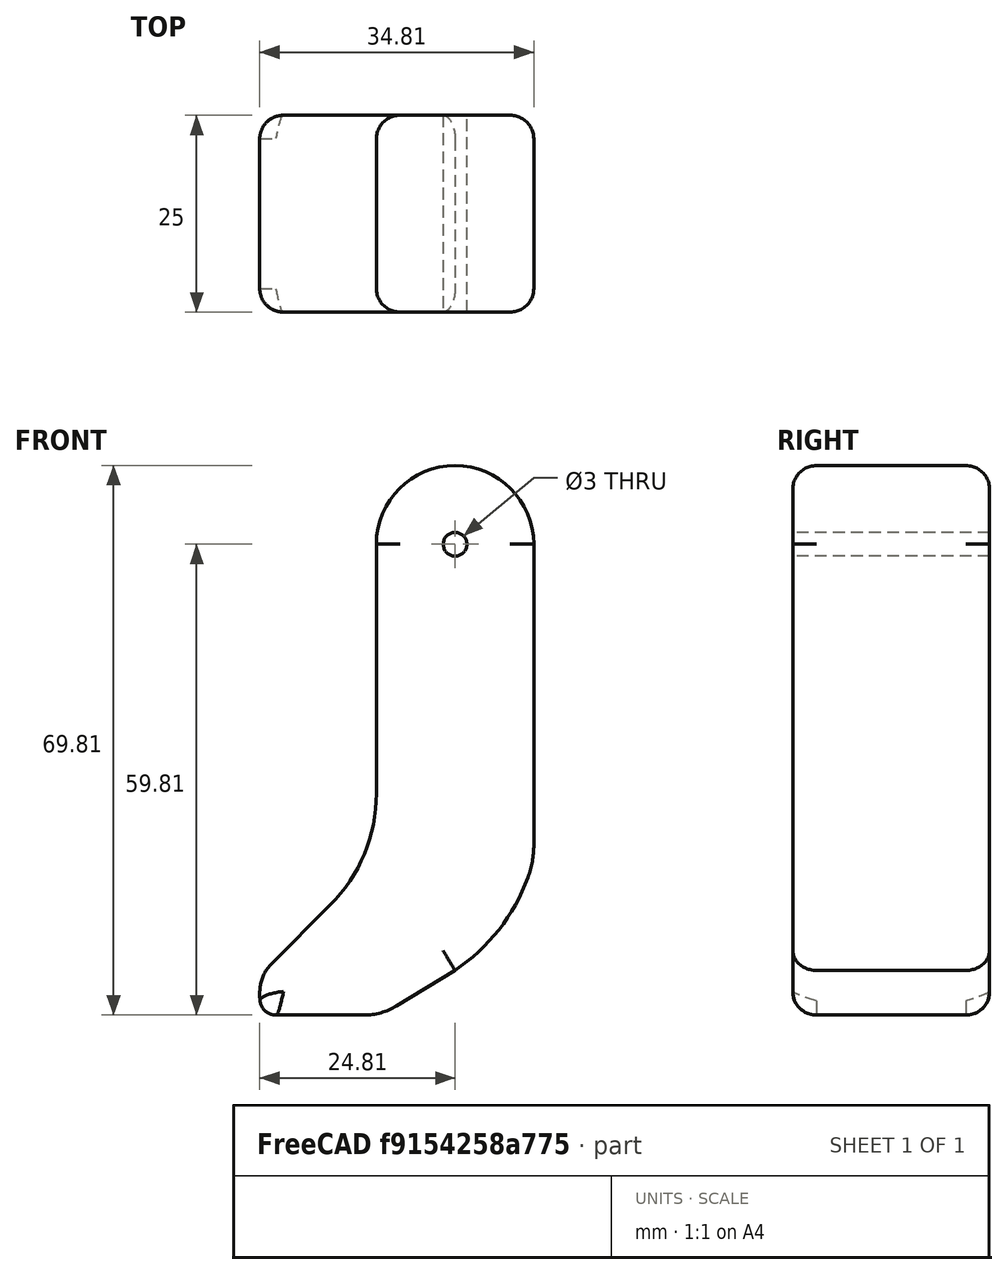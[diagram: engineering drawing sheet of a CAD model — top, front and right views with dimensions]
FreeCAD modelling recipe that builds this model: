
FCSTD DOCUMENT  (FreeCAD 1.0R38806 (Git))
Label: pata
License: All rights reserved
LicenseURL: https://en.wikipedia.org/wiki/All_rights_reserved
objects: PartDesign::Fillet×7, TechDraw::DrawProjGroupItem×5, TechDraw::DrawViewDimension×5, Sketcher::SketchObject×2, TechDraw::DrawProjGroup×2, PartDesign::Pad×1, TechDraw::DrawSVGTemplate×1, PartDesign::Pocket×1, PartDesign::Body×1, App::Part×1, TechDraw::DrawPage×1
note: 37 computed .brp shape members not serialized (recipe doc carries the construction recipe); baked Part::Feature solids carry a one-line shape summary decoded from their .brp

FEATURE [Sketcher::SketchObject] Sketch  label="Sketch_pata_15mm"
  ArcFitTolerance = 1e-06
  AttachmentSupport = -> [XZ_Plane001]
  FullyConstrained = false
  MakeInternals = false
  MapMode = 5
  Placement = pos=(0,0,0) rot=(1,0,0;1.5708rad)
  sketch-geometry (8):
    g0: LineSegment StartX=-10.0001 StartY=23.058 StartZ=0 EndX=-10.0001 EndY=-16.942 EndZ=0
    g1: LineSegment StartX=9.99968 StartY=23.058 StartZ=0 EndX=9.99968 EndY=-16.942 EndZ=0
    g2: LineSegment StartX=-10.0001 StartY=-16.942 StartZ=0 EndX=-24.1423 EndY=-31.0842 EndZ=0
    g3: ArcOfCircle CenterX=-17.3511 CenterY=-34.1744 CenterZ=0 NormalX=0 NormalY=0 NormalZ=1 AngleXU=0 Radius=7.46124 StartAngle=2.71455 EndAngle=3.49995
    g4: LineSegment StartX=-24.3383 StartY=-36.7914 StartZ=0 EndX=-9.33834 EndY=-36.7914 EndZ=0
    g5: LineSegment StartX=-9.33834 StartY=-36.7914 StartZ=0 EndX=-1.8e-15 EndY=-31.1116 EndZ=0
    g6: ArcOfCircle CenterX=-13.6431 CenterY=-10.8702 CenterZ=0 NormalX=0 NormalY=0 NormalZ=1 AngleXU=0 Radius=24.41 StartAngle=5.30546 EndAngle=6.0318
    g7: ArcOfCircle CenterX=-0.000231101 CenterY=23.0162 CenterZ=0 NormalX=0 NormalY=0 NormalZ=1 AngleXU=0 Radius=10 StartAngle=0.00417804 EndAngle=3.13741
  constraints (21):
    c: Distance(g0) = 40
    c: Vertical(g0)
    c: Distance(g1) = 40
    c: Vertical(g1)
    c: Distance(g2) = 20
    c: Angle(g-1,g2) = -2.35619
    c: Coincident(g2,g0)
    c: Angle(g3) = 0.785398
    c: Coincident(g3,g2)
    c: Distance(g4) = 15
    c: Horizontal(g4)
    c: Coincident(g4,g3)
    c: Coincident(g5,g4)
    c: PointOnObject(g5,g-2)
    c: Coincident(g6,g5)
    c: Coincident(g6,g1)
    c: Coincident(g7,g1)
    c: Coincident(g7,g0)
    c: Radius(g7) = 10
    c: Distance(g5,g5) = 10.93
    c: Radius(g6) = 24.41
FEATURE [PartDesign::Pad] Pad
  Direction = (0,-1,2e-16)
  Length = 25
  Length2 = 10
  Placement = pos=(0,0,0) rot=(1,0,0;1.5708rad)
  Profile = -> Sketch
  ReferenceAxis = -> Sketch [N_Axis]
  Refine = true
  Suppressed = false
  Type = 0
FEATURE [PartDesign::Fillet] Fillet
  Base = -> Pad [Edge11]
  BaseFeature = -> Pad
  Placement = pos=(0,0,0) rot=(1,0,0;1.5708rad)
  Radius = 2
  Refine = true
  SupportTransform = false
  Suppressed = false
  UseAllEdges = false
FEATURE [PartDesign::Fillet] Fillet001
  Base = -> Fillet [Edge23]
  BaseFeature = -> Fillet
  Placement = pos=(0,0,0) rot=(1,0,0;1.5708rad)
  Radius = 8
  Refine = true
  SupportTransform = false
  Suppressed = false
  UseAllEdges = false
FEATURE [PartDesign::Fillet] Fillet002
  Base = -> Fillet001 [Edge20]
  BaseFeature = -> Fillet001
  Placement = pos=(0,0,0) rot=(1,0,0;1.5708rad)
  Radius = 5
  Refine = true
  SupportTransform = false
  Suppressed = false
  UseAllEdges = false
FEATURE [PartDesign::Fillet] Fillet003
  Base = -> Fillet002 [Edge31]
  BaseFeature = -> Fillet002
  Placement = pos=(0,0,0) rot=(1,0,0;1.5708rad)
  Radius = 12
  Refine = true
  SupportTransform = false
  Suppressed = false
  UseAllEdges = false
FEATURE [PartDesign::Fillet] Fillet004
  Base = -> Fillet003 [Edge22]
  BaseFeature = -> Fillet003
  Placement = pos=(0,0,0) rot=(1,0,0;1.5708rad)
  Radius = 20
  Refine = true
  SupportTransform = false
  Suppressed = false
  UseAllEdges = false
FEATURE [PartDesign::Fillet] Fillet005
  Base = -> Fillet004 [Edge20]
  BaseFeature = -> Fillet004
  Placement = pos=(0,0,0) rot=(1,0,0;1.5708rad)
  Radius = 3
  Refine = true
  SupportTransform = false
  Suppressed = false
  UseAllEdges = false
FEATURE [PartDesign::Fillet] Fillet006
  Base = -> Fillet005 [Edge11]
  BaseFeature = -> Fillet005
  Placement = pos=(0,0,0) rot=(1,0,0;1.5708rad)
  Radius = 3
  Refine = true
  SupportTransform = false
  Suppressed = false
  UseAllEdges = false
FEATURE [TechDraw::DrawSVGTemplate] Template
  EditableTexts = approval_person=Mecatrónica; creator=A.Mrtz, N.Grc, T.Marí; date_of_issue=12/14/24; document_status=In preparation; document_type=Assembly Drawing; drawing_number=DN; general_tolerances=ISO 2768-m; language_code=EN; part_material=Stainless steel Mat.No. 1.4301; responsible_department=RD; revision_index=AAA; sheet_number=1 / 1; sheet_scale=1 : 1; title=Pierna_ajolote
  Height = 297
  Orientation = 1
  Template = <path>
  Width = 420
FEATURE [Sketcher::SketchObject] Sketch001
  ArcFitTolerance = 1e-06
  AttachmentSupport = -> [Fillet006]
  FullyConstrained = false
  MakeInternals = false
  MapMode = 5
  Placement = pos=(0,-25,0) rot=(1,0,0;1.5708rad)
  sketch-geometry (1):
    g0: Circle CenterX=0 CenterY=23.02 CenterZ=0 NormalX=0 NormalY=0 NormalZ=1 AngleXU=0 Radius=1.5
  constraints (2):
    c: Diameter(g0) = 3
    c: PointOnObject(g0,g-2)
FEATURE [PartDesign::Pocket] Pocket
  BaseFeature = -> Fillet006
  Direction = (0,1,-2e-16)
  Length = 5
  Length2 = 5
  Placement = pos=(0,0,0) rot=(1,0,0;1.5708rad)
  Profile = -> Sketch001
  ReferenceAxis = -> Sketch001 [N_Axis]
  Refine = true
  Suppressed = false
  Type = 1
FEATURE [PartDesign::Body] Body  label="Pata"
  AllowCompound = false
  Group = -> [Sketch,Pad,Fillet,Fillet001,Fillet002,Fillet003,Fillet004,Fillet005,Fillet006,Sketch001,Pocket]
  Origin = -> Origin001
  Tip = -> Pocket
FEATURE [App::Part] Part  label="Pata001"
  Group = -> [Body]
  Origin = -> Origin
FEATURE [TechDraw::DrawProjGroupItem] ProjItem003  label="Top"
  CoarseView = false
  Direction = (0,0,1)
  Focus = 100
  HardHidden = false
  IsoCount = 0
  IsoHidden = false
  IsoVisible = false
  LockPosition = false
  Perspective = false
  Rotation = 0
  RotationVector = (1,0,0)
  ScaleType = 0
  ScrubCount = 1
  SeamHidden = false
  SeamVisible = false
  SmoothHidden = false
  SmoothVisible = true
  Source = -> [Body]
  Type = 4
  X = 0
  XDirection = (1,0,0)
  Y = -109.808
FEATURE [TechDraw::DrawProjGroupItem] ProjItem  label="Front"
  CoarseView = false
  Direction = (0,-1,0)
  Focus = 100
  HardHidden = false
  IsoCount = 0
  IsoHidden = false
  IsoVisible = false
  LockPosition = true
  Perspective = false
  Rotation = 0
  RotationVector = (1,0,0)
  Scale = 2
  ScaleType = 2
  ScrubCount = 1
  SeamHidden = false
  SeamVisible = false
  SmoothHidden = false
  SmoothVisible = true
  Source = -> [Body]
  Type = 0
  X = 0
  XDirection = (1,0,0)
  Y = 0
FEATURE [TechDraw::DrawProjGroupItem] ProjItem004  label="Top001"
  CoarseView = false
  Direction = (0,0,1)
  Focus = 100
  HardHidden = false
  IsoCount = 0
  IsoHidden = false
  IsoVisible = false
  LockPosition = false
  Perspective = false
  Rotation = 0
  RotationVector = (1,0,0)
  Scale = 2
  ScaleType = 2
  ScrubCount = 1
  SeamHidden = false
  SeamVisible = false
  SmoothHidden = false
  SmoothVisible = true
  Source = -> [Body]
  Type = 4
  X = 0
  XDirection = (1,0,0)
  Y = -109.808
FEATURE [TechDraw::DrawProjGroupItem] ProjItem005  label="Right"
  CoarseView = false
  Direction = (1,-1e-16,0)
  Focus = 100
  HardHidden = false
  IsoCount = 0
  IsoHidden = false
  IsoVisible = false
  LockPosition = false
  Perspective = false
  Rotation = 0
  RotationVector = (1,0,0)
  Scale = 2
  ScaleType = 2
  ScrubCount = 1
  SeamHidden = false
  SeamVisible = false
  SmoothHidden = false
  SmoothVisible = true
  Source = -> [Body]
  Type = 2
  X = -74.812
  XDirection = (1e-16,1,0)
  Y = 0
FEATURE [TechDraw::DrawProjGroup] ProjGroup
  Anchor = -> ProjItem
  AutoDistribute = true
  LockPosition = false
  ProjectionType = 0
  Rotation = 0
  Scale = 2
  ScaleType = 2
  Source = -> [Body]
  Views = -> [ProjItem,ProjItem004,ProjItem005]
  X = 163.14
  Y = 185.495
  spacingX = 15
  spacingY = 15
FEATURE [TechDraw::DrawProjGroupItem] ProjItem006  label="Front001"
  CoarseView = false
  Direction = (-0.542357,-0.811005,0.21936)
  Focus = 100
  HardHidden = false
  IsoCount = 0
  IsoHidden = false
  IsoVisible = false
  LockPosition = true
  Perspective = false
  Rotation = 0
  RotationVector = (0.829017,-0.558968,-0.0168809)
  Scale = 2
  ScaleType = 2
  ScrubCount = 1
  SeamHidden = false
  SeamVisible = false
  SmoothHidden = false
  SmoothVisible = true
  Source = -> [Part]
  Type = 0
  X = 0
  XDirection = (0.829017,-0.558968,-0.0168809)
  Y = 0
FEATURE [TechDraw::DrawProjGroup] ProjGroup001
  Anchor = -> ProjItem006
  AutoDistribute = true
  LockPosition = false
  ProjectionType = 0
  Rotation = 0
  Scale = 2
  ScaleType = 2
  Source = -> [Part]
  Views = -> [ProjItem006]
  X = 315.642
  Y = 180.562
  spacingX = 15
  spacingY = 15
FEATURE [TechDraw::DrawViewDimension] Dimension
  AngleOverride = false
  Arbitrary = false
  ArbitraryTolerances = false
  BoxCorners = (2) [(-25,-69.8076,-1e-07),(25,69.8076,1e-07)]
  EqualTolerance = true
  ExtensionAngle = 0
  FormatSpec = %.2w
  FormatSpecOverTolerance = %+.2w
  FormatSpecUnderTolerance = %+.2w
  Inverted = false
  LineAngle = 0
  LockPosition = false
  MeasureType = 1
  OverTolerance = 0
  References2D = -> [ProjItem005]
  Rotation = 0
  ScaleType = 0
  TheoreticalExact = false
  Type = 1
  UnderTolerance = 0
  X = 0
  Y = 86.8968
FEATURE [TechDraw::DrawViewDimension] Dimension003
  AngleOverride = false
  Arbitrary = false
  ArbitraryTolerances = false
  BoxCorners = (2) [(-34.812,-69.8076,-1e-07),(34.812,69.8076,1e-07)]
  EqualTolerance = true
  ExtensionAngle = 0
  FormatSpec = R%.2w
  FormatSpecOverTolerance = %+.2w
  FormatSpecUnderTolerance = %+.2w
  Inverted = false
  LineAngle = 0
  LockPosition = false
  MeasureType = 1
  OverTolerance = 0
  References2D = -> [ProjItem]
  Rotation = 0
  ScaleType = 0
  TheoreticalExact = false
  Type = 4
  UnderTolerance = 0
  X = 39.7018
  Y = 82.7862
FEATURE [TechDraw::DrawViewDimension] Dimension004
  AngleOverride = false
  Arbitrary = false
  ArbitraryTolerances = false
  BoxCorners = (2) [(-34.812,-69.8076,-1e-07),(34.812,69.8076,1e-07)]
  EqualTolerance = true
  ExtensionAngle = 0
  FormatSpec = R%.2w
  FormatSpecOverTolerance = %+.2w
  FormatSpecUnderTolerance = %+.2w
  Inverted = false
  LineAngle = 0
  LockPosition = false
  MeasureType = 1
  OverTolerance = 0
  References2D = -> [ProjItem]
  Rotation = 0
  ScaleType = 0
  TheoreticalExact = false
  Type = 4
  UnderTolerance = 0
  X = 11.2159
  Y = 87.7189
FEATURE [TechDraw::DrawViewDimension] Dimension005
  AngleOverride = false
  Arbitrary = false
  ArbitraryTolerances = false
  BoxCorners = (2) [(-34.812,-25,-1e-07),(34.812,25,1e-07)]
  EqualTolerance = true
  ExtensionAngle = 0
  FormatSpec = R%.2w
  FormatSpecOverTolerance = %+.2w
  FormatSpecUnderTolerance = %+.2w
  Inverted = false
  LineAngle = 0
  LockPosition = false
  MeasureType = 1
  OverTolerance = 0
  References2D = -> [ProjItem004]
  Rotation = 0
  ScaleType = 0
  TheoreticalExact = false
  Type = 4
  UnderTolerance = 0
  X = 45.4652
  Y = 42.1471
FEATURE [TechDraw::DrawViewDimension] Dimension006
  AngleOverride = false
  Arbitrary = false
  ArbitraryTolerances = false
  BoxCorners = (2) [(-34.812,-69.8076,-1e-07),(34.812,69.8076,1e-07)]
  EqualTolerance = true
  ExtensionAngle = 0
  FormatSpec = ⌀%.2w
  FormatSpecOverTolerance = %+.2w
  FormatSpecUnderTolerance = %+.2w
  Inverted = false
  LineAngle = 0
  LockPosition = false
  MeasureType = 1
  OverTolerance = 0
  References2D = -> [ProjItem]
  Rotation = 0
  ScaleType = 0
  TheoreticalExact = false
  Type = 5
  UnderTolerance = 0
  X = 48.4984
  Y = 32.784
FEATURE [TechDraw::DrawPage] Page
  KeepUpdated = true
  NextBalloonIndex = 1
  ProjectionType = 0
  Template = -> Template
  Views = -> [ProjGroup,ProjGroup001,Dimension,Dimension003,Dimension004,Dimension005,Dimension006]
note: 1 file-system path scrubbed to <path> (originals preserved in the JSON sidecar)
